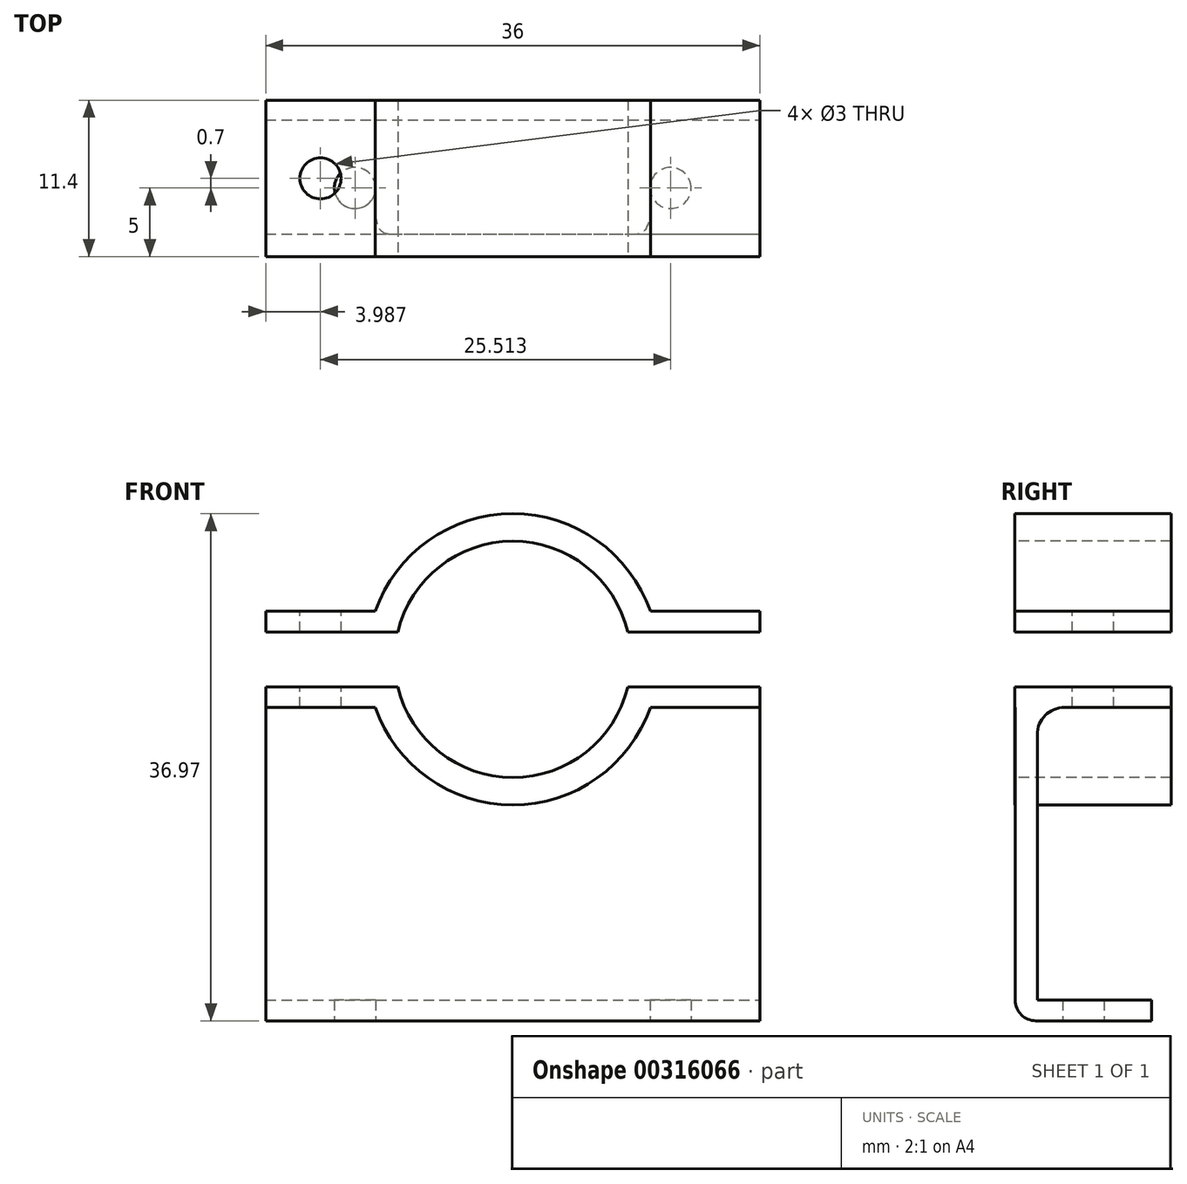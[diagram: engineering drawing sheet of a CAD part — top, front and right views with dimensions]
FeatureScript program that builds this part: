
annotation { "Feature Type Name" : "Feature", "Feature Type Description" : "" }
export const myFeature = defineFeature(function(context is Context, id is Id, definition is map)
    precondition{}
    {
        {
            var Q0;
            Q0=qCreatedBy(makeId("Top.planeOp"),FACE);
            var sketch = newSketch(context, id + "F0", { "sketchPlane" : qUnion([Q0])});
            skCircle(sketch, "E0", {"center": v(-11.5, 0) * mm, "radius": 1.5 * mm});
            skCircle(sketch, "E1", {"center": v(11.5, 0) * mm, "radius": 1.5 * mm});
            skLineSegment(sketch, "E2", {"start": v(-11.5, 0) * mm, "end": v(11.5, 0) * mm, "construction": true});
            skPoint(sketch, "E3", {"position": v(0, 0) * mm});
            skLineSegment(sketch, "E4.bottom", {"start": v(-18, -4.96) * mm, "end": v(18, -4.96) * mm});
            skLineSegment(sketch, "E4.top", {"start": v(-18, 4.96) * mm, "end": v(18, 4.96) * mm});
            skLineSegment(sketch, "E4.left", {"start": v(-18, -4.96) * mm, "end": v(-18, 4.96) * mm});
            skLineSegment(sketch, "E4.right", {"start": v(18, -4.96) * mm, "end": v(18, 4.96) * mm});
            skLineSegment(sketch, "E5", {"start": v(-11.5, 0) * mm, "end": v(-18, 0) * mm, "construction": true});
            skLineSegment(sketch, "E6", {"start": v(11.5, 0) * mm, "end": v(18, 0) * mm, "construction": true});
            skLineSegment(sketch, "E7", {"start": v(-11.5, 0) * mm, "end": v(-11.5, -4.96) * mm, "construction": true});
            skLineSegment(sketch, "E8", {"start": v(-11.5, 0) * mm, "end": v(-11.5, 4.96) * mm, "construction": true});
            skSolve(sketch);
        }
        {
            var Q0;
            Q0=makeQuery(id+"F0.imprint","IMPRINT",FACE,{"disambiguationData":[TD([[makeQuery(id+"F0.imprint","IMPRINT",EDGE,{"derivedFrom":sQuery(id+"F0.wireOp",EDGE,"E0")}),-1.0]])]});
            extrude(context, id + "F1", {"entities" : qUnion([Q0]), "depth" : 1.5 * mm});
        }
        {
            var Q0;
            Q0=makeQuery(id+"F1.opExtrude","CAP_FACE",FACE,{"disambiguationData":[OSD([sQuery(id+"F0.wireOp",EDGE,"E0"),sQuery(id+"F0.wireOp",EDGE,"E1"),sQuery(id+"F0.wireOp",EDGE,"E4.bottom"),sQuery(id+"F0.wireOp",EDGE,"E4.top"),sQuery(id+"F0.wireOp",EDGE,"E4.left"),sQuery(id+"F0.wireOp",EDGE,"E4.right")])],"isStart":false});
            var sketch = newSketch(context, id + "F2", { "sketchPlane" : qUnion([Q0])});
            skLineSegment(sketch, "E9.bottom", {"start": v(-18, -4.96) * mm, "end": v(18, -4.96) * mm});
            skLineSegment(sketch, "E9.top", {"start": v(-18, -3.36) * mm, "end": v(18, -3.36) * mm});
            skLineSegment(sketch, "E9.left", {"start": v(-18, -4.96) * mm, "end": v(-18, -3.36) * mm});
            skLineSegment(sketch, "E9.right", {"start": v(18, -4.96) * mm, "end": v(18, -3.36) * mm});
            skSolve(sketch);
        }
        {
            var Q0;
            Q0=qCreatedBy(makeId("Front.planeOp"),FACE);
            var sketch = newSketch(context, id + "F3", { "sketchPlane" : qUnion([Q0])});
            skArc(sketch, "E10", {"start": v(-7.53, 25.16) * mm, "mid": v(0, 18.73) * mm, "end": v(7.53, 25.16) * mm, "construction": true});
            skArc(sketch, "E11.0", {"start": v(-8.38, 24.35) * mm, "mid": v(0, 17.73) * mm, "end": v(8.38, 24.35) * mm});
            skArc(sketch, "E12.trimOffspring", {"start": v(7.53, 25.16) * mm, "mid": v(0, 33.97) * mm, "end": v(-7.53, 25.16) * mm, "construction": true});
            skArc(sketch, "E13.trimOffspring", {"start": v(8.38, 28.35) * mm, "mid": v(0, 34.97) * mm, "end": v(-8.38, 28.35) * mm});
            skArc(sketch, "E14", {"start": v(-10.43, 24.35) * mm, "mid": v(0, 15.73) * mm, "end": v(10.43, 24.35) * mm});
            skLineSegment(sketch, "E15.bottom", {"start": v(18, 28.35) * mm, "end": v(7.35, 28.35) * mm});
            skLineSegment(sketch, "E15.top", {"start": v(18, 24.35) * mm, "end": v(7.35, 24.35) * mm});
            skLineSegment(sketch, "E16.bottom", {"start": v(18, 29.85) * mm, "end": v(6.77, 29.85) * mm});
            skLineSegment(sketch, "E16.top", {"start": v(18, 22.85) * mm, "end": v(6.77, 22.85) * mm});
            skLineSegment(sketch, "E16.left", {"start": v(18, 29.85) * mm, "end": v(18, 28.35) * mm});
            skLineSegment(sketch, "E16.right", {"start": v(-18, 29.85) * mm, "end": v(-18, 28.35) * mm});
            skLineSegment(sketch, "E17.trimOffspring", {"start": v(-18, 24.35) * mm, "end": v(-18, 22.85) * mm});
            skLineSegment(sketch, "E18.trimOffspring", {"start": v(18, 24.35) * mm, "end": v(18, 22.85) * mm});
            skArc(sketch, "E19.trimOffspring", {"start": v(10.43, 28.35) * mm, "mid": v(0, 36.97) * mm, "end": v(-10.43, 28.35) * mm});
            skLineSegment(sketch, "E20.trimOffspring", {"start": v(-7.35, 28.35) * mm, "end": v(-18, 28.35) * mm});
            skLineSegment(sketch, "E21.trimOffspring", {"start": v(-7.35, 24.35) * mm, "end": v(-18, 24.35) * mm});
            skLineSegment(sketch, "E22.trimOffspring", {"start": v(-6.77, 22.85) * mm, "end": v(-18, 22.85) * mm});
            skLineSegment(sketch, "E23.trimOffspring", {"start": v(-6.77, 29.85) * mm, "end": v(-18, 29.85) * mm});
            skSolve(sketch);
        }
        {
            var Q0;
            Q0=qSketchRegion(id+"F3",true);
            extrude(context, id + "F4", {"entities" : qUnion([Q0]), "operationType" : NewBodyOperationType.ADD, "oppositeDirection" : true, "depth" : 6.4 * mm, "hasSecondDirection" : true, "secondDirectionOppositeDirection" : false, "secondDirectionDepth" : 5 * mm});
        }
        {
            var Q0;
            Q0=makeQuery(id+"F1.opExtrude","SWEPT_FACE",FACE,{"disambiguationData":[OSD([sQuery(id+"F0.wireOp",EDGE,"E4.bottom")])]});
            var sketch = newSketch(context, id + "F5", { "sketchPlane" : qUnion([Q0])});
            skLineSegment(sketch, "E24", {"start": v(-18, 0) * mm, "end": v(-18, 41.07) * mm});
            skLineSegment(sketch, "E25", {"start": v(-18, 41.07) * mm, "end": v(18, 41.07) * mm});
            skLineSegment(sketch, "E26", {"start": v(18, 41.07) * mm, "end": v(18, 1.5) * mm});
            skSolve(sketch);
        }
        {
            var Q0;
            {var subQ2=sQuery(id+"F5.wireOp",EDGE,"E25");Q0=makeQuery(id+"F5.imprint","IMPRINT",FACE,{"disambiguationData":[TD([[makeQuery(id+"F5.imprint","IMPRINT",EDGE,{"derivedFrom":subQ2}),-1.0]])]});}
            extrude(context, id + "F6", {"entities" : qUnion([Q0]), "operationType" : NewBodyOperationType.ADD, "oppositeDirection" : true, "depth" : 1.6 * mm});
        }
        {
            var Q0;
            Q0=makeQuery(id+"F1.opExtrude","CAP_EDGE",EDGE,{"disambiguationData":[OSD([sQuery(id+"F0.wireOp",EDGE,"E4.bottom")])],"isStart":true});
            var Q1;
            Q1=makeQuery(id+"F6.opExtrude","CAP_EDGE",EDGE,{"disambiguationData":[OSD([sQuery(id+"F0.wireOp",EDGE,"E4.bottom")])],"isStart":false});
            fillet(context, id + "F7", {"entities" : qUnion([Q0, Q1]), "radius" : 1.5 * mm, "tangentPropagation" : true, "allowEdgeOverflow" : false});
        }
        {
            var Q0;
            Q0=makeQuery(id+"F6.boolean.opBoolean","SPLIT",FACE,{"derivedFrom":makeQuery(id+"F6.opExtrude","CAP_FACE",FACE,{"disambiguationData":[OSD([sQuery(id+"F0.wireOp",EDGE,"E4.bottom"),sQuery(id+"F5.wireOp",EDGE,"E24"),sQuery(id+"F5.wireOp",EDGE,"E25"),sQuery(id+"F5.wireOp",EDGE,"E26")])],"isStart":true})});
            extrude(context, id + "F8", {"entities" : qUnion([Q0]), "operationType" : NewBodyOperationType.REMOVE, "oppositeDirection" : true, "depth" : 25 * mm});
        }
        {
            var Q0;
            Q0=makeQuery(id+"FlOMhzXWSGImMCi_1.imprint","IMPRINT",FACE,{"disambiguationData":[TD([[makeQuery(id+"FlOMhzXWSGImMCi_1.imprint","IMPRINT",EDGE,{"derivedFrom":sQuery(id+"FlOMhzXWSGImMCi_1.wireOp",EDGE,"IvtVsbHx-eB6J-AR4h-rlWi-ziGurIT2tkif")}),1.0]])]});
            var Q1;
            Q1=makeQuery(id+"F2.imprint","IMPRINT",FACE,{"disambiguationData":[TD([[makeQuery(id+"F2.imprint","IMPRINT",EDGE,{"derivedFrom":sQuery(id+"F2.wireOp",EDGE,"E9.bottom")}),1.0]])]});
            var Q2;
            Q2=sQuery(id+"FlOMhzXWSGImMCi_1.wireOp",EDGE,"IvtVsbHx-eB6J-AR4h-rlWi-ziGurIT2tkif");
            extrude(context, id + "F9", {"entities" : qUnion([Q0, Q1]), "operationType" : NewBodyOperationType.ADD, "surfaceEntities" : qUnion([Q2]), "depth" : 22 * mm});
        }
        {
            var Q0;
            Q0=makeQuery(id+"F6.boolean.opBoolean","INTERSECT",EDGE,{"derivedFrom":[makeQuery(id+"F4.opExtrude","SWEPT_FACE",FACE,{"disambiguationData":[OSD([sQuery(id+"F3.wireOp",EDGE,"E22.trimOffspring")])]}),makeQuery(id+"F6.opExtrude","CAP_FACE",FACE,{"disambiguationData":[OSD([sQuery(id+"F0.wireOp",EDGE,"E4.bottom"),sQuery(id+"F5.wireOp",EDGE,"E24"),sQuery(id+"F5.wireOp",EDGE,"E25"),sQuery(id+"F5.wireOp",EDGE,"E26")])],"isStart":false})]});
            var Q1;
            Q1=makeQuery(id+"F6.boolean.opBoolean","INTERSECT",EDGE,{"derivedFrom":[makeQuery(id+"F4.opExtrude","SWEPT_FACE",FACE,{"disambiguationData":[OSD([sQuery(id+"F3.wireOp",EDGE,"E16.top")])]}),makeQuery(id+"F6.opExtrude","CAP_FACE",FACE,{"disambiguationData":[OSD([sQuery(id+"F0.wireOp",EDGE,"E4.bottom"),sQuery(id+"F5.wireOp",EDGE,"E24"),sQuery(id+"F5.wireOp",EDGE,"E25"),sQuery(id+"F5.wireOp",EDGE,"E26")])],"isStart":false})]});
            fillet(context, id + "F10", {"entities" : qUnion([Q0, Q1]), "radius" : 2 * mm, "tangentPropagation" : true, "allowEdgeOverflow" : false});
        }
        {
            var Q0;
            Q0=makeQuery(id+"F9.opExtrude","SWEPT_FACE",FACE,{"disambiguationData":[OSD([sQuery(id+"F2.wireOp",EDGE,"E9.bottom")])]});
            extrude(context, id + "F11", {"entities" : qUnion([Q0]), "operationType" : NewBodyOperationType.REMOVE, "oppositeDirection" : true, "depth" : 25 * mm});
        }
        {
            var Q0;
            {var subQ0=sQuery(id+"F5.wireOp",EDGE,"E26");var subQ1=sQuery(id+"F5.wireOp",EDGE,"E25");var subQ2=sQuery(id+"F5.wireOp",EDGE,"E24");var subQ3=sQuery(id+"F3.wireOp",EDGE,"E23.trimOffspring");var subQ4=sQuery(id+"F0.wireOp",EDGE,"E4.bottom");var subQ17=makeQuery(id+"F4.opExtrude","SWEPT_FACE",FACE,{"disambiguationData":[OSD([subQ3])]});Q0=makeQuery(id+"F8.boolean.opBoolean","MERGE",FACE,{"derivedFrom":[makeQuery(id+"F6.boolean.opBoolean","SPLIT",FACE,{"disambiguationData":[TD([makeQuery(id+"F6.opExtrude","CAP_FACE",FACE,{"disambiguationData":[OSD([subQ4,subQ2,subQ1,subQ0])],"isStart":true})])],"derivedFrom":subQ17}),makeQuery(id+"F6.boolean.opBoolean","SPLIT",FACE,{"disambiguationData":[TD([makeQuery(id+"F6.opExtrude","CAP_FACE",FACE,{"disambiguationData":[OSD([subQ4,subQ2,subQ1,subQ0])],"isStart":false})])],"derivedFrom":subQ17}),makeQuery(id+"F8.opExtrude","SWEPT_FACE",FACE,{"disambiguationData":[OSD([subQ4,subQ3,subQ2,subQ1,subQ0])]})]});}
            var sketch = newSketch(context, id + "F12", { "sketchPlane" : qUnion([Q0])});
            skCircle(sketch, "E27", {"center": v(-14.01, 0.7) * mm, "radius": 1.5 * mm});
            skPoint(sketch, "E27.centerSnap0", {"position": v(-14.01, -5) * mm});
            skPoint(sketch, "E27.centerSnap1", {"position": v(-10.03, 0.7) * mm});
            skCircle(sketch, "E28.MirrorC", {"center": v(14.01, 0.7) * mm, "radius": 1.5 * mm});
            skSolve(sketch);
        }
        {
            var Q0;
            Q0=makeQuery(id+"F12.imprint","IMPRINT",FACE,{"disambiguationData":[TD([[makeQuery(id+"F12.imprint","IMPRINT",EDGE,{"derivedFrom":sQuery(id+"F12.wireOp",EDGE,"E27")}),1.0]])]});
            var Q1;
            Q1=makeQuery(id+"F12.imprint","IMPRINT",FACE,{"disambiguationData":[TD([[makeQuery(id+"F12.imprint","IMPRINT",EDGE,{"derivedFrom":sQuery(id+"F12.wireOp",EDGE,"E28.MirrorC")}),-1.0]])]});
            var Q2;
            Q2=makeQuery(id+"F1.opExtrude","CAP_FACE",FACE,{"disambiguationData":[OSD([sQuery(id+"F0.wireOp",EDGE,"E0"),sQuery(id+"F0.wireOp",EDGE,"E1"),sQuery(id+"F0.wireOp",EDGE,"E4.bottom"),sQuery(id+"F0.wireOp",EDGE,"E4.top"),sQuery(id+"F0.wireOp",EDGE,"E4.left"),sQuery(id+"F0.wireOp",EDGE,"E4.right")])],"isStart":false});
            extrude(context, id + "F13", {"entities" : qUnion([Q0, Q1]), "operationType" : NewBodyOperationType.REMOVE, "endBound" : BoundingType.UP_TO_SURFACE, "oppositeDirection" : true, "endBoundEntityFace" : qUnion([Q2]), "depth" : 25 * mm});
        }
    });
